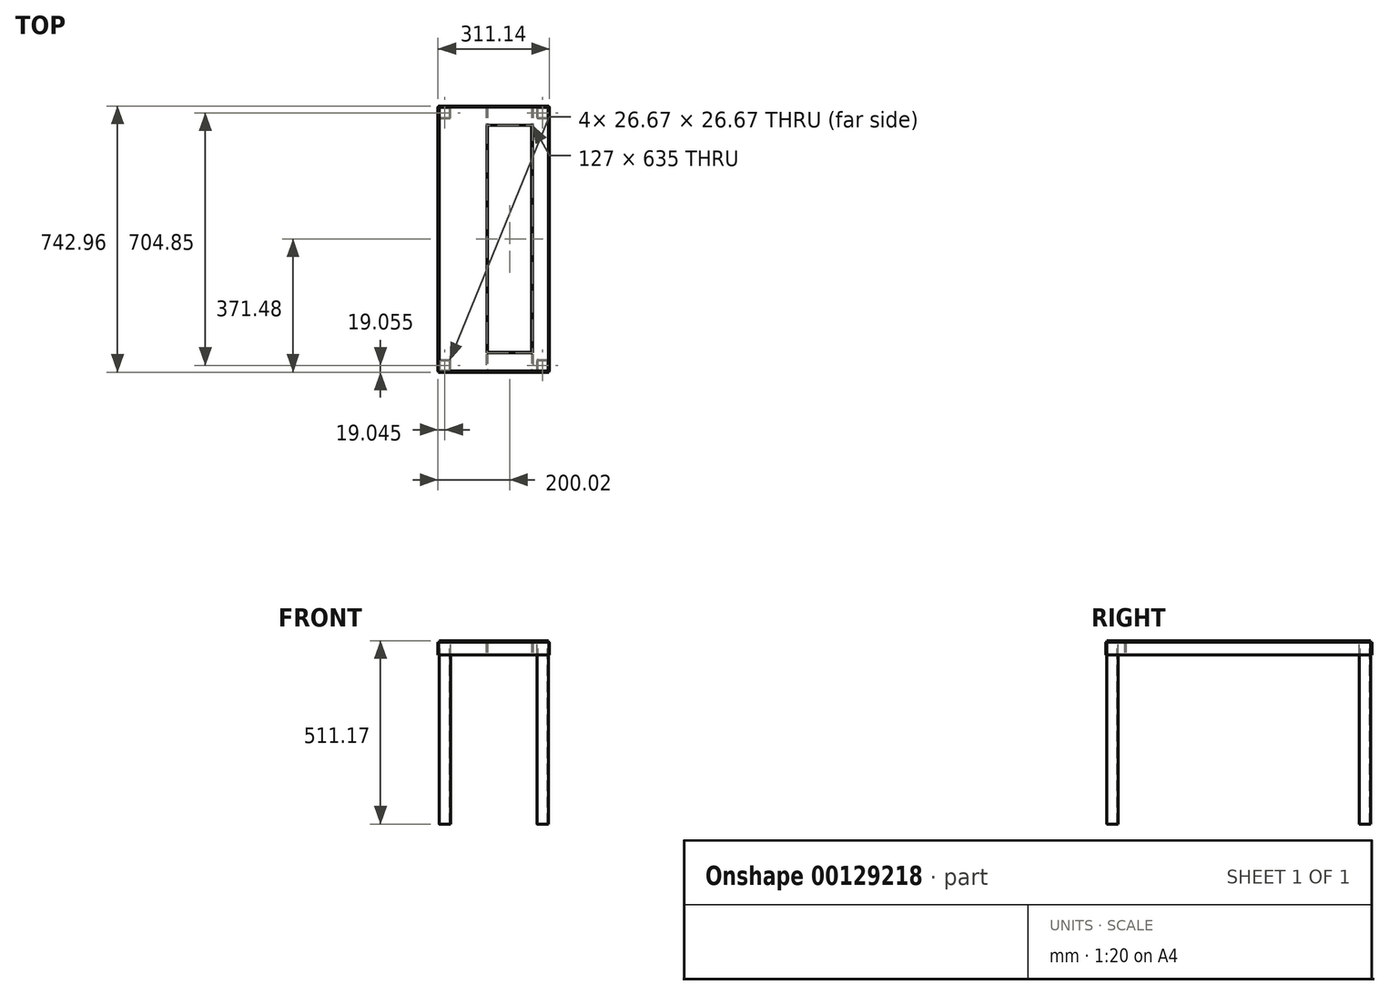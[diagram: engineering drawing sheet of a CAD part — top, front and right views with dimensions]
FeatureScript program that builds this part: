
annotation { "Feature Type Name" : "Feature", "Feature Type Description" : "" }
export const myFeature = defineFeature(function(context is Context, id is Id, definition is map)
    precondition{}
    {
        {
            var Q0;
            Q0=qCreatedBy(makeId("Top.planeOp"),FACE);
            var sketch = newSketch(context, id + "F0", { "sketchPlane" : qUnion([Q0])});
            skLineSegment(sketch, "E0.bottom", {"start": v(152.4, -368.3) * mm, "end": v(-152.4, -368.3) * mm});
            skLineSegment(sketch, "E0.top", {"start": v(152.4, 368.3) * mm, "end": v(-152.4, 368.3) * mm});
            skLineSegment(sketch, "E0.left", {"start": v(152.4, -368.3) * mm, "end": v(152.4, 368.3) * mm});
            skLineSegment(sketch, "E0.right", {"start": v(-152.4, -368.3) * mm, "end": v(-152.4, 368.3) * mm});
            skPoint(sketch, "E0.middle", {"position": v(0, 0) * mm});
            skLineSegment(sketch, "E1.bottom", {"start": v(-19.05, 317.5) * mm, "end": v(107.95, 317.5) * mm});
            skLineSegment(sketch, "E1.top", {"start": v(-19.05, -317.5) * mm, "end": v(107.95, -317.5) * mm});
            skLineSegment(sketch, "E1.left", {"start": v(-19.05, 317.5) * mm, "end": v(-19.05, -317.5) * mm});
            skLineSegment(sketch, "E1.right", {"start": v(107.95, 317.5) * mm, "end": v(107.95, -317.5) * mm});
            skSolve(sketch);
        }
        {
            var Q0;
            Q0 = qSketchRegion(id + "F0", true);
            extrude(context, id + "F1", {"entities" : qUnion([Q0]), "depth" : 3.17 * mm});
        }
        {
            var Q0;
            Q0=makeQuery(id+"F1.opExtrude","SWEPT_FACE",FACE,{"disambiguationData":[OSD([sQuery(id+"F0.wireOp",EDGE,"E0.left")])]});
            var sketch = newSketch(context, id + "F2", { "sketchPlane" : qUnion([Q0])});
            skLineSegment(sketch, "E2.bottom", {"start": v(-368.3, 1.59) * mm, "end": v(368.3, 1.59) * mm});
            skLineSegment(sketch, "E2.top", {"start": v(-368.3, -36.51) * mm, "end": v(368.3, -36.51) * mm});
            skLineSegment(sketch, "E2.left", {"start": v(-368.3, 1.59) * mm, "end": v(-368.3, -36.51) * mm});
            skLineSegment(sketch, "E2.right", {"start": v(368.3, 1.59) * mm, "end": v(368.3, -36.51) * mm});
            skSolve(sketch);
        }
        {
            var Q0;
            {var subQ0=sQuery(id+"F2.wireOp",EDGE,"E2.top");Q0=makeQuery(id+"F2.imprint","IMPRINT",FACE,{"disambiguationData":[TD([[makeQuery(id+"F2.imprint","IMPRINT",EDGE,{"derivedFrom":subQ0}),1.0]])]});}
            extrude(context, id + "F3", {"entities" : qUnion([Q0]), "depth" : 3.17 * mm});
        }
        {
            var Q0;
            Q0=makeQuery(id+"F3.opExtrude","SWEPT_BODY",BODY,{"disambiguationData":[OSD([sQuery(id+"F0.wireOp",EDGE,"E0.left"),sQuery(id+"F2.wireOp",EDGE,"E2.top"),sQuery(id+"F2.wireOp",EDGE,"E2.left"),sQuery(id+"F2.wireOp",EDGE,"E2.right")])]});
            var Q1;
            Q1=qCreatedBy(makeId("Right.planeOp"),FACE);
            mirror(context, id + "F4", {"entities" : qUnion([Q0]), "mirrorPlane" : qUnion([Q1])});
        }
        {
            var Q0;
            Q0=makeQuery(id+"F1.opExtrude","SWEPT_FACE",FACE,{"disambiguationData":[OSD([sQuery(id+"F0.wireOp",EDGE,"E0.bottom")])]});
            var sketch = newSketch(context, id + "F5", { "sketchPlane" : qUnion([Q0])});
            skLineSegment(sketch, "E3.0", {"start": v(-155.58, 0) * mm, "end": v(-152.4, 0) * mm, "construction": true});
            skLineSegment(sketch, "E4.0", {"start": v(155.57, 0) * mm, "end": v(152.4, 0) * mm, "construction": true});
            skPoint(sketch, "E5.oppositeSnap0", {"position": v(153.99, 0) * mm});
            skLineSegment(sketch, "E5.bottom", {"start": v(-153.99, 0) * mm, "end": v(153.99, 0) * mm});
            skLineSegment(sketch, "E5.top", {"start": v(-153.99, -36.51) * mm, "end": v(153.99, -36.51) * mm});
            skLineSegment(sketch, "E5.left", {"start": v(-153.99, 0) * mm, "end": v(-153.99, -36.51) * mm});
            skLineSegment(sketch, "E5.right", {"start": v(153.99, 0) * mm, "end": v(153.99, -36.51) * mm});
            skLineSegment(sketch, "E6.0", {"start": v(155.57, -36.51) * mm, "end": v(152.4, -36.51) * mm, "construction": true});
            skPoint(sketch, "E7", {"position": v(153.99, -36.51) * mm});
            skSolve(sketch);
        }
        {
            var Q0;
            Q0 = qSketchRegion(id + "F5", true);
            extrude(context, id + "F6", {"entities" : qUnion([Q0]), "depth" : 3.17 * mm});
        }
        {
            var Q0;
            Q0=makeQuery(id+"F6.opExtrude","SWEPT_BODY",BODY,{"disambiguationData":[OSD([sQuery(id+"F5.wireOp",EDGE,"E5.bottom"),sQuery(id+"F5.wireOp",EDGE,"E5.top"),sQuery(id+"F5.wireOp",EDGE,"E5.left"),sQuery(id+"F5.wireOp",EDGE,"E5.right")])]});
            var Q1;
            Q1=qCreatedBy(makeId("Front.planeOp"),FACE);
            mirror(context, id + "F7", {"entities" : qUnion([Q0]), "mirrorPlane" : qUnion([Q1])});
        }
        {
            var Q0;
            Q0=qCreatedBy(makeId("Right.planeOp"),FACE);
            var Q1;
            Q1=makeQuery(id+"F1.opExtrude","CAP_EDGE",EDGE,{"disambiguationData":[OSD([sQuery(id+"F0.wireOp",EDGE,"E1.left")])],"isStart":true});
            cPlane(context, id + "F8", {"entities" : qUnion([Q0, Q1]), "cplaneType" : CPlaneType.LINE_ANGLE, "offset" : 22.86 * mm, "angle" : 0 * degree, "width" : 152.4 * mm, "height" : 152.4 * mm});
        }
        {
            var Q0;
            Q0=qCreatedBy(id+"F8.planeOp",FACE);
            var sketch = newSketch(context, id + "F9", { "sketchPlane" : qUnion([Q0])});
            skLineSegment(sketch, "E8", {"start": v(-368.3, 0) * mm, "end": v(-368.3, -36.51) * mm, "construction": true});
            skLineSegment(sketch, "E9", {"start": v(368.3, 0) * mm, "end": v(317.5, 0) * mm, "construction": true});
            skLineSegment(sketch, "E10", {"start": v(-317.5, 0) * mm, "end": v(-368.3, 0) * mm, "construction": true});
            skLineSegment(sketch, "E11", {"start": v(368.3, -36.51) * mm, "end": v(368.3, 0) * mm, "construction": true});
            skLineSegment(sketch, "E12.bottom", {"start": v(-368.3, 0) * mm, "end": v(368.3, 0) * mm});
            skLineSegment(sketch, "E12.top", {"start": v(-368.3, -36.51) * mm, "end": v(368.3, -36.51) * mm});
            skLineSegment(sketch, "E12.left", {"start": v(368.3, 0) * mm, "end": v(368.3, -36.51) * mm});
            skLineSegment(sketch, "E12.right", {"start": v(-368.3, 0) * mm, "end": v(-368.3, -36.51) * mm});
            skSolve(sketch);
        }
        {
            var Q0;
            Q0 = qSketchRegion(id + "F9", true);
            extrude(context, id + "F10", {"entities" : qUnion([Q0]), "depth" : 3.17 * mm, "symmetric" : true});
        }
        {
            var Q0;
            Q0=makeQuery(id+"F1.opExtrude","CAP_EDGE",EDGE,{"disambiguationData":[OSD([sQuery(id+"F0.wireOp",EDGE,"E1.right")])],"isStart":true});
            cPlane(context, id + "F11", {"entities" : qUnion([Q0]), "cplaneType" : CPlaneType.LINE_ANGLE, "offset" : 25.4 * mm, "angle" : 90 * degree, "width" : 152.4 * mm, "height" : 152.4 * mm});
        }
        {
            var Q0;
            Q0=qCreatedBy(id+"F11.planeOp",FACE);
            var sketch = newSketch(context, id + "F12", { "sketchPlane" : qUnion([Q0])});
            skLineSegment(sketch, "E13", {"start": v(368.3, -36.51) * mm, "end": v(368.3, 0) * mm, "construction": true});
            skLineSegment(sketch, "E14", {"start": v(-317.5, 0) * mm, "end": v(-368.3, 0) * mm, "construction": true});
            skLineSegment(sketch, "E15", {"start": v(317.5, 0) * mm, "end": v(-317.5, 0) * mm});
            skLineSegment(sketch, "E16", {"start": v(368.3, 0) * mm, "end": v(317.5, 0) * mm, "construction": true});
            skLineSegment(sketch, "E17", {"start": v(-368.3, 0) * mm, "end": v(-368.3, -36.51) * mm, "construction": true});
            skLineSegment(sketch, "E18.bottom", {"start": v(368.3, 0) * mm, "end": v(-368.3, 0) * mm});
            skLineSegment(sketch, "E18.top", {"start": v(368.3, -36.51) * mm, "end": v(-368.3, -36.51) * mm});
            skLineSegment(sketch, "E18.left", {"start": v(368.3, 0) * mm, "end": v(368.3, -36.51) * mm});
            skLineSegment(sketch, "E18.right", {"start": v(-368.3, 0) * mm, "end": v(-368.3, -36.51) * mm});
            skSolve(sketch);
        }
        {
            var Q0;
            Q0 = qSketchRegion(id + "F12", true);
            extrude(context, id + "F13", {"entities" : qUnion([Q0]), "depth" : 3.17 * mm, "symmetric" : true});
        }
        {
            var Q0;
            Q0=makeQuery(id+"F1.opExtrude","CAP_EDGE",EDGE,{"disambiguationData":[OSD([sQuery(id+"F0.wireOp",EDGE,"E1.top")])],"isStart":true});
            cPlane(context, id + "F14", {"entities" : qUnion([Q0]), "cplaneType" : CPlaneType.LINE_ANGLE, "offset" : 25.4 * mm, "angle" : 0 * degree, "width" : 152.4 * mm, "height" : 152.4 * mm});
        }
        {
            var Q0;
            Q0=qCreatedBy(id+"F14.planeOp",FACE);
            var sketch = newSketch(context, id + "F15", { "sketchPlane" : qUnion([Q0])});
            skLineSegment(sketch, "E19", {"start": v(17.46, -36.51) * mm, "end": v(17.46, 0) * mm});
            skLineSegment(sketch, "E20", {"start": v(-106.36, 0) * mm, "end": v(-106.36, -36.51) * mm});
            skLineSegment(sketch, "E21", {"start": v(-106.36, -36.51) * mm, "end": v(17.46, -36.51) * mm});
            skLineSegment(sketch, "E22", {"start": v(17.46, 0) * mm, "end": v(-106.36, 0) * mm});
            skSolve(sketch);
        }
        {
            var Q0;
            Q0 = qSketchRegion(id + "F15", true);
            extrude(context, id + "F16", {"entities" : qUnion([Q0]), "oppositeDirection" : true, "depth" : 3.17 * mm, "symmetric" : true});
        }
        {
            var Q0;
            Q0=makeQuery(id+"F1.opExtrude","CAP_FACE",FACE,{"disambiguationData":[OSD([sQuery(id+"F0.wireOp",EDGE,"E0.bottom"),sQuery(id+"F0.wireOp",EDGE,"E0.top"),sQuery(id+"F0.wireOp",EDGE,"E0.left"),sQuery(id+"F0.wireOp",EDGE,"E0.right"),sQuery(id+"F0.wireOp",EDGE,"E1.bottom"),sQuery(id+"F0.wireOp",EDGE,"E1.top"),sQuery(id+"F0.wireOp",EDGE,"E1.left"),sQuery(id+"F0.wireOp",EDGE,"E1.right")])],"isStart":true});
            var sketch = newSketch(context, id + "F17", { "sketchPlane" : qUnion([Q0])});
            skLineSegment(sketch, "E23.bottom", {"start": v(-149.23, 368.3) * mm, "end": v(-123.83, 368.3) * mm});
            skLineSegment(sketch, "E23.top", {"start": v(-149.22, 336.55) * mm, "end": v(-123.82, 336.55) * mm});
            skLineSegment(sketch, "E23.left", {"start": v(-152.4, 365.13) * mm, "end": v(-152.4, 339.73) * mm});
            skLineSegment(sketch, "E23.right", {"start": v(-120.65, 365.13) * mm, "end": v(-120.65, 339.73) * mm});
            skPoint(sketch, "E24.visualSharp", {"position": v(-120.65, 368.3) * mm});
            skArc(sketch, "E24.filletArc", {"start": v(-120.65, 365.13) * mm, "mid": v(-121.58, 367.37) * mm, "end": v(-123.83, 368.3) * mm});
            skPoint(sketch, "E25.visualSharp", {"position": v(-120.65, 336.55) * mm});
            skArc(sketch, "E25.filletArc", {"start": v(-123.82, 336.55) * mm, "mid": v(-121.58, 337.48) * mm, "end": v(-120.65, 339.73) * mm});
            skPoint(sketch, "E26.visualSharp", {"position": v(-152.4, 336.55) * mm});
            skArc(sketch, "E26.filletArc", {"start": v(-152.4, 339.73) * mm, "mid": v(-151.47, 337.48) * mm, "end": v(-149.22, 336.55) * mm});
            skPoint(sketch, "E27.visualSharp", {"position": v(-152.4, 368.3) * mm});
            skArc(sketch, "E27.filletArc", {"start": v(-149.23, 368.3) * mm, "mid": v(-151.47, 367.37) * mm, "end": v(-152.4, 365.13) * mm});
            skLineSegment(sketch, "E28.0", {"start": v(-149.86, 365.76) * mm, "end": v(-149.86, 339.1) * mm});
            skLineSegment(sketch, "E28.1", {"start": v(-149.86, 365.76) * mm, "end": v(-123.19, 365.76) * mm});
            skLineSegment(sketch, "E28.2", {"start": v(-123.19, 365.76) * mm, "end": v(-123.19, 339.1) * mm});
            skLineSegment(sketch, "E28.3", {"start": v(-149.86, 339.1) * mm, "end": v(-123.19, 339.1) * mm});
            skLineSegment(sketch, "E29.0.1.0", {"start": v(-123.19, -339.09) * mm, "end": v(-123.19, -365.76) * mm});
            skLineSegment(sketch, "E29.0.1.1", {"start": v(-149.86, -365.76) * mm, "end": v(-123.19, -365.76) * mm});
            skPoint(sketch, "E29.0.1.2", {"position": v(-152.4, -336.55) * mm});
            skLineSegment(sketch, "E29.0.1.3", {"start": v(-120.65, -339.72) * mm, "end": v(-120.65, -365.12) * mm});
            skPoint(sketch, "E29.0.1.4", {"position": v(-120.65, -336.55) * mm});
            skLineSegment(sketch, "E29.0.1.5", {"start": v(-149.22, -368.3) * mm, "end": v(-123.82, -368.3) * mm});
            skPoint(sketch, "E29.0.1.6", {"position": v(-120.65, -368.3) * mm});
            skPoint(sketch, "E29.0.1.7", {"position": v(-152.4, -368.3) * mm});
            skLineSegment(sketch, "E29.0.1.8", {"start": v(-149.86, -339.09) * mm, "end": v(-123.19, -339.09) * mm});
            skLineSegment(sketch, "E29.0.1.9", {"start": v(-149.86, -339.09) * mm, "end": v(-149.86, -365.76) * mm});
            skLineSegment(sketch, "E29.0.1.10", {"start": v(-152.4, -339.72) * mm, "end": v(-152.4, -365.12) * mm});
            skLineSegment(sketch, "E29.0.1.11", {"start": v(-149.23, -336.55) * mm, "end": v(-123.83, -336.55) * mm});
            skArc(sketch, "E29.0.1.12", {"start": v(-152.4, -365.12) * mm, "mid": v(-151.47, -367.37) * mm, "end": v(-149.22, -368.3) * mm});
            skArc(sketch, "E29.0.1.13", {"start": v(-123.82, -368.3) * mm, "mid": v(-121.58, -367.37) * mm, "end": v(-120.65, -365.12) * mm});
            skArc(sketch, "E29.0.1.14", {"start": v(-149.23, -336.55) * mm, "mid": v(-151.47, -337.48) * mm, "end": v(-152.4, -339.72) * mm});
            skArc(sketch, "E29.0.1.15", {"start": v(-120.65, -339.72) * mm, "mid": v(-121.58, -337.48) * mm, "end": v(-123.83, -336.55) * mm});
            skLineSegment(sketch, "E29.1.0.0", {"start": v(149.67, 365.76) * mm, "end": v(149.67, 339.1) * mm});
            skLineSegment(sketch, "E29.1.0.1", {"start": v(123, 339.1) * mm, "end": v(149.67, 339.1) * mm});
            skPoint(sketch, "E29.1.0.2", {"position": v(120.46, 368.3) * mm});
            skLineSegment(sketch, "E29.1.0.3", {"start": v(152.2, 365.13) * mm, "end": v(152.2, 339.73) * mm});
            skPoint(sketch, "E29.1.0.4", {"position": v(152.2, 368.3) * mm});
            skLineSegment(sketch, "E29.1.0.5", {"start": v(123.63, 336.55) * mm, "end": v(149.03, 336.55) * mm});
            skPoint(sketch, "E29.1.0.6", {"position": v(152.2, 336.55) * mm});
            skPoint(sketch, "E29.1.0.7", {"position": v(120.46, 336.55) * mm});
            skLineSegment(sketch, "E29.1.0.8", {"start": v(123, 365.76) * mm, "end": v(149.67, 365.76) * mm});
            skLineSegment(sketch, "E29.1.0.9", {"start": v(123, 365.76) * mm, "end": v(123, 339.1) * mm});
            skLineSegment(sketch, "E29.1.0.10", {"start": v(120.46, 365.13) * mm, "end": v(120.46, 339.73) * mm});
            skLineSegment(sketch, "E29.1.0.11", {"start": v(123.63, 368.3) * mm, "end": v(149.03, 368.3) * mm});
            skArc(sketch, "E29.1.0.12", {"start": v(120.46, 339.73) * mm, "mid": v(121.39, 337.48) * mm, "end": v(123.63, 336.55) * mm});
            skArc(sketch, "E29.1.0.13", {"start": v(149.03, 336.55) * mm, "mid": v(151.28, 337.48) * mm, "end": v(152.2, 339.73) * mm});
            skArc(sketch, "E29.1.0.14", {"start": v(123.63, 368.3) * mm, "mid": v(121.39, 367.37) * mm, "end": v(120.46, 365.13) * mm});
            skArc(sketch, "E29.1.0.15", {"start": v(152.2, 365.13) * mm, "mid": v(151.28, 367.37) * mm, "end": v(149.03, 368.3) * mm});
            skLineSegment(sketch, "E29.1.1.0", {"start": v(149.67, -339.09) * mm, "end": v(149.67, -365.76) * mm});
            skLineSegment(sketch, "E29.1.1.1", {"start": v(123, -365.76) * mm, "end": v(149.67, -365.76) * mm});
            skPoint(sketch, "E29.1.1.2", {"position": v(120.46, -336.55) * mm});
            skLineSegment(sketch, "E29.1.1.3", {"start": v(152.2, -339.72) * mm, "end": v(152.2, -365.12) * mm});
            skPoint(sketch, "E29.1.1.4", {"position": v(152.2, -336.55) * mm});
            skLineSegment(sketch, "E29.1.1.5", {"start": v(123.63, -368.3) * mm, "end": v(149.03, -368.3) * mm});
            skPoint(sketch, "E29.1.1.6", {"position": v(152.2, -368.3) * mm});
            skPoint(sketch, "E29.1.1.7", {"position": v(120.46, -368.3) * mm});
            skLineSegment(sketch, "E29.1.1.8", {"start": v(123, -339.09) * mm, "end": v(149.67, -339.09) * mm});
            skLineSegment(sketch, "E29.1.1.9", {"start": v(123, -339.09) * mm, "end": v(123, -365.76) * mm});
            skLineSegment(sketch, "E29.1.1.10", {"start": v(120.46, -339.72) * mm, "end": v(120.46, -365.12) * mm});
            skLineSegment(sketch, "E29.1.1.11", {"start": v(123.63, -336.55) * mm, "end": v(149.03, -336.55) * mm});
            skArc(sketch, "E29.1.1.12", {"start": v(120.46, -365.12) * mm, "mid": v(121.39, -367.37) * mm, "end": v(123.63, -368.3) * mm});
            skArc(sketch, "E29.1.1.13", {"start": v(149.03, -368.3) * mm, "mid": v(151.28, -367.37) * mm, "end": v(152.2, -365.12) * mm});
            skArc(sketch, "E29.1.1.14", {"start": v(123.63, -336.55) * mm, "mid": v(121.39, -337.48) * mm, "end": v(120.46, -339.72) * mm});
            skArc(sketch, "E29.1.1.15", {"start": v(152.2, -339.72) * mm, "mid": v(151.28, -337.48) * mm, "end": v(149.03, -336.55) * mm});
            skLineSegment(sketch, "E29.direction1", {"start": v(-152.4, 336.55) * mm, "end": v(120.46, 336.55) * mm, "construction": true});
            skLineSegment(sketch, "E29.direction2", {"start": v(-152.4, 336.55) * mm, "end": v(-152.4, -368.3) * mm, "construction": true});
            skSolve(sketch);
        }
        {
            var Q0;
            Q0 = qSketchRegion(id + "F17", true);
            extrude(context, id + "F18", {"entities" : qUnion([Q0]), "depth" : 508 * mm});
        }
    });
